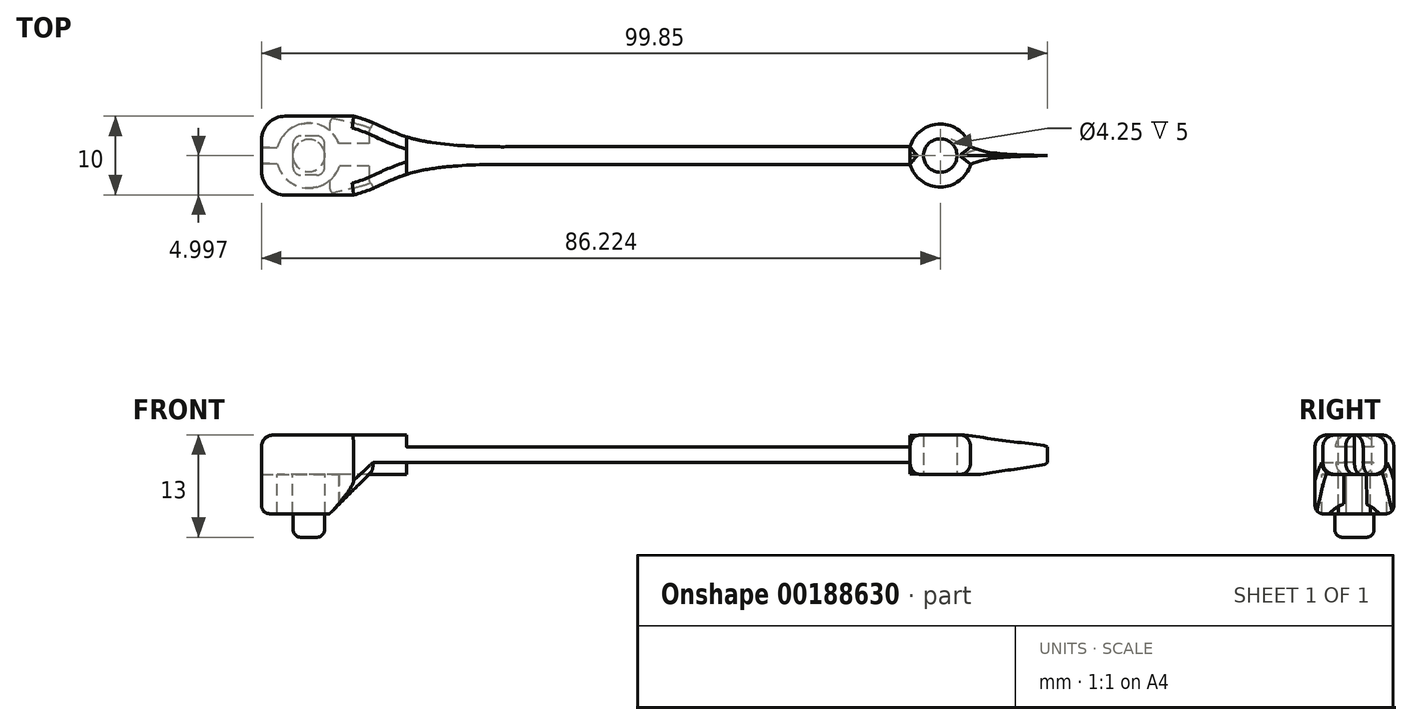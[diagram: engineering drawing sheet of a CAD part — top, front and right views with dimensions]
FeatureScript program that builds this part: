
annotation { "Feature Type Name" : "Feature", "Feature Type Description" : "" }
export const myFeature = defineFeature(function(context is Context, id is Id, definition is map)
    precondition{}
    {
        {
            var Q0;
            Q0=qCreatedBy(makeId("Top.planeOp"),FACE);
            var sketch = newSketch(context, id + "F0", { "sketchPlane" : qUnion([Q0])});
            skLineSegment(sketch, "E0.right", {"start": v(-50, 3.04) * mm, "end": v(-50, -0.96) * mm});
            skPoint(sketch, "E0.middle", {"position": v(0, 1.04) * mm});
            skLineSegment(sketch, "E1.bottom", {"start": v(-47, 6.04) * mm, "end": v(-38, 6.04) * mm});
            skLineSegment(sketch, "E1.top", {"start": v(-47, -3.96) * mm, "end": v(-38, -3.96) * mm});
            skLineSegment(sketch, "E1.right", {"start": v(-38, 6.04) * mm, "end": v(-38, 5.96) * mm});
            skFitSpline(sketch, "E2.MirrorCS", {"points": [v(-38.32, 6.04) * mm, v(-30.88, 3.21) * mm, v(-1.67, 3.16) * mm, v(36.22, 5.93) * mm, v(49.85, 2.13) * mm], "startDerivative": vector(52.94, -12.3) * mm, "endDerivative": vector(42.84, -21) * mm});
            skLineSegment(sketch, "E3.trimOffspring", {"start": v(-38, 6.04) * mm, "end": v(-47, 6.04) * mm});
            skPoint(sketch, "E4.orphan", {"position": v(50, 6.04) * mm});
            skLineSegment(sketch, "E5.trimOffspring", {"start": v(-38, -3.96) * mm, "end": v(-47, -3.96) * mm});
            skPoint(sketch, "E6.visualSharp", {"position": v(-50, 6.04) * mm});
            skArc(sketch, "E6.filletArc", {"start": v(-47, 6.04) * mm, "mid": v(-49.12, 5.16) * mm, "end": v(-50, 3.04) * mm});
            skPoint(sketch, "E7.visualSharp", {"position": v(-50, -3.96) * mm});
            skArc(sketch, "E7.filletArc", {"start": v(-50, -0.96) * mm, "mid": v(-49.12, -3.08) * mm, "end": v(-47, -3.96) * mm});
            skLineSegment(sketch, "E8", {"start": v(-18.95, 2.15) * mm, "end": v(32.38, 2.15) * mm});
            skFitSpline(sketch, "E9.MirrorCS", {"points": [v(-38.32, -3.97) * mm, v(-30.88, -1.14) * mm, v(-1.67, -1.09) * mm, v(36.22, -3.86) * mm, v(49.85, -0.06) * mm], "startDerivative": vector(52.94, 12.3) * mm, "endDerivative": vector(42.84, 21) * mm});
            skLineSegment(sketch, "E10.MirrorCS", {"start": v(-18.95, -0.08) * mm, "end": v(32.38, -0.08) * mm});
            skArc(sketch, "E11", {"start": v(40.06, 2.15) * mm, "mid": v(36.22, 5.04) * mm, "end": v(32.38, 2.15) * mm});
            skFitSpline(sketch, "E12", {"points": [v(40.06, 2.15) * mm, v(42.27, 1.49) * mm, v(49.85, 1.04) * mm], "startDerivative": vector(5.23, -2.09) * mm, "endDerivative": vector(13.53, -0.32) * mm});
            skFitSpline(sketch, "E13.MirrorCS", {"points": [v(40.06, -0.08) * mm, v(42.27, 0.59) * mm, v(49.85, 1.04) * mm], "startDerivative": vector(5.23, 2.09) * mm, "endDerivative": vector(13.53, 0.32) * mm});
            skCircle(sketch, "E14", {"center": v(36.22, 1.04) * mm, "radius": 2.12 * mm});
            skLineSegment(sketch, "E15.trimOffspring", {"start": v(40.06, -0.08) * mm, "end": v(49.84, -0.08) * mm});
            skArc(sketch, "E16.trimOffspring", {"start": v(32.38, -0.08) * mm, "mid": v(36.22, -2.96) * mm, "end": v(40.06, -0.08) * mm});
            skPoint(sketch, "E17.trimOffspring.end.orphan", {"position": v(49.84, 2.15) * mm});
            skPoint(sketch, "E18.start.orphan", {"position": v(-38, 1.04) * mm});
            skLineSegment(sketch, "E19.trimOffspring", {"start": v(-38, -3.89) * mm, "end": v(-38, -3.96) * mm});
            skPoint(sketch, "E20.startSnap0", {"position": v(-50, 1.04) * mm});
            skCircle(sketch, "E21", {"center": v(-43.9, 1.04) * mm, "radius": 2.12 * mm});
            skPoint(sketch, "E20.start.orphan", {"position": v(-49.8, 1.04) * mm});
            skSolve(sketch);
        }
        {
            var Q0;
            Q0=makeQuery(id+"F0.imprint","IMPRINT",FACE,{"disambiguationData":[TD([[makeQuery(id+"F0.imprint","IMPRINT",EDGE,{"derivedFrom":sQuery(id+"F0.wireOp",EDGE,"E0.right")}),1.0]])]});
            var Q1;
            Q1=makeQuery(id+"F0.imprint","IMPRINT",FACE,{"disambiguationData":[TD([[makeQuery(id+"F0.imprint","IMPRINT",EDGE,{"derivedFrom":sQuery(id+"F0.wireOp",EDGE,"E21")}),1.0]])]});
            extrude(context, id + "F1", {"entities" : qUnion([Q0, Q1]), "depth" : 5 * mm});
        }
        {
            var Q0;
            Q0=makeQuery(id+"F1.opExtrude","CAP_FACE",FACE,{"disambiguationData":[OSD([sQuery(id+"F0.wireOp",EDGE,"E0.right"),sQuery(id+"F0.wireOp",EDGE,"E2.MirrorCS"),sQuery(id+"F0.wireOp",EDGE,"E3.trimOffspring"),sQuery(id+"F0.wireOp",EDGE,"E5.trimOffspring"),sQuery(id+"F0.wireOp",EDGE,"E6.filletArc"),sQuery(id+"F0.wireOp",EDGE,"E7.filletArc"),sQuery(id+"F0.wireOp",EDGE,"E8"),sQuery(id+"F0.wireOp",EDGE,"E9.MirrorCS"),sQuery(id+"F0.wireOp",EDGE,"E10.MirrorCS"),sQuery(id+"F0.wireOp",EDGE,"E11"),sQuery(id+"F0.wireOp",EDGE,"E12"),sQuery(id+"F0.wireOp",EDGE,"E13.MirrorCS"),sQuery(id+"F0.wireOp",EDGE,"E14"),sQuery(id+"F0.wireOp",EDGE,"E16.trimOffspring")])],"isStart":false});
            var sketch = newSketch(context, id + "F2", { "sketchPlane" : qUnion([Q0])});
            skCircle(sketch, "E22", {"center": v(-44, 1.04) * mm, "radius": 2.05 * mm});
            skPoint(sketch, "E23.start.orphan", {"position": v(-50, 1.04) * mm});
            skPoint(sketch, "E24.trimOffspring.end.orphan", {"position": v(-37.98, 1.04) * mm});
            skArc(sketch, "E25", {"start": v(-40.17, 2.59) * mm, "mid": v(-48.12, 0.91) * mm, "end": v(-40.08, -0.28) * mm});
            skLineSegment(sketch, "E26", {"start": v(-35.34, 4.98) * mm, "end": v(-35.34, 2.53) * mm});
            skLineSegment(sketch, "E27.trimOffspring", {"start": v(-35.34, -0.28) * mm, "end": v(-35.34, -3.64) * mm});
            skLineSegment(sketch, "E28.0", {"start": v(-35.34, 2.53) * mm, "end": v(-40.17, 2.59) * mm});
            skLineSegment(sketch, "E29.0", {"start": v(-35.34, -0.28) * mm, "end": v(-40.08, -0.28) * mm});
            skSolve(sketch);
        }
        {
            var Q0;
            Q0 = qSketchRegion(id + "F2", true);
            var Q1;
            {var subQ2=sQuery(id+"F2.wireOp",EDGE,"E25");Q1=makeQuery(id+"F2.imprint","IMPRINT",FACE,{"disambiguationData":[TD([[makeQuery(id+"F2.imprint","IMPRINT",EDGE,{"derivedFrom":subQ2}),-1.0]])]});}
            extrude(context, id + "F3", {"entities" : qUnion([Q0, Q1]), "operationType" : NewBodyOperationType.ADD, "oppositeDirection" : true, "depth" : 10 * mm});
        }
        {
            var Q0;
            Q0=makeQuery(id+"F3.opExtrude","CAP_FACE",FACE,{"disambiguationData":[OSD([sQuery(id+"F2.wireOp",EDGE,"E22")])],"isStart":false});
            var sketch = newSketch(context, id + "F4", { "sketchPlane" : qUnion([Q0])});
            skLineSegment(sketch, "E30.bottom", {"start": v(-42, 1.46) * mm, "end": v(-46, 1.46) * mm});
            skLineSegment(sketch, "E30.top", {"start": v(-42, -3.54) * mm, "end": v(-46, -3.54) * mm});
            skLineSegment(sketch, "E30.left", {"start": v(-42, 1.46) * mm, "end": v(-42, -3.54) * mm});
            skLineSegment(sketch, "E30.right", {"start": v(-46, 1.46) * mm, "end": v(-46, -3.54) * mm});
            skPoint(sketch, "E30.middle", {"position": v(-44, -1.04) * mm});
            skSolve(sketch);
        }
        {
            var Q0;
            {var subQ0=sQuery(id+"F4.wireOp",EDGE,"E30.bottom");Q0=makeQuery(id+"F4.imprint","IMPRINT",FACE,{"disambiguationData":[TD([[makeQuery(id+"F4.imprint","IMPRINT",EDGE,{"derivedFrom":subQ0}),1.0]])]});}
            var Q1;
            {var subQ0=sQuery(id+"F4.wireOp",EDGE,"E30.top");Q1=makeQuery(id+"F4.imprint","IMPRINT",FACE,{"disambiguationData":[TD([[makeQuery(id+"F4.imprint","IMPRINT",EDGE,{"derivedFrom":subQ0}),-1.0]])]});}
            var Q2;
            {var subQ0=sQuery(id+"F4.wireOp",EDGE,"E30.left");var subQ1=makeQuery(id+"F3.opExtrude","CAP_EDGE",EDGE,{"disambiguationData":[OSD([sQuery(id+"F2.wireOp",EDGE,"E22")])],"isStart":false});var subQ2=makeQuery(id+"F4.imprint","INTERSECT",VERTEX,{"disambiguationData":[OD(0.0)],"derivedFrom":[subQ1,subQ0]});Q2=makeQuery(id+"F4.imprint","IMPRINT",FACE,{"disambiguationData":[TD([[makeQuery(id+"F4.imprint","IMPRINT",EDGE,{"disambiguationData":[TD([[subQ2,-1.0]])],"derivedFrom":subQ0}),-1.0]])]});}
            extrude(context, id + "F5", {"entities" : qUnion([Q0, Q1, Q2]), "operationType" : NewBodyOperationType.ADD, "depth" : 3 * mm});
        }
        {
            var Q0;
            Q0=makeQuery(id+"F5.opExtrude","CAP_EDGE",EDGE,{"disambiguationData":[OSD([sQuery(id+"F4.wireOp",EDGE,"E30.top")])],"isStart":false});
            var Q1;
            Q1=makeQuery(id+"F5.opExtrude","CAP_EDGE",EDGE,{"disambiguationData":[OSD([sQuery(id+"F4.wireOp",EDGE,"E30.right")])],"isStart":false});
            var Q2;
            Q2=makeQuery(id+"F5.opExtrude","CAP_EDGE",EDGE,{"disambiguationData":[OSD([sQuery(id+"F4.wireOp",EDGE,"E30.left")])],"isStart":false});
            var Q3;
            Q3=makeQuery(id+"F5.opExtrude","CAP_EDGE",EDGE,{"disambiguationData":[OSD([sQuery(id+"F4.wireOp",EDGE,"E30.bottom")])],"isStart":false});
            fillet(context, id + "F6", {"entities" : qUnion([Q0, Q1, Q2, Q3]), "radius" : 1 * mm, "tangentPropagation" : true, "allowEdgeOverflow" : false});
        }
        {
            var Q0;
            Q0=makeQuery(id+"F5.opExtrude","SWEPT_EDGE",EDGE,{"disambiguationData":[OSD([sQuery(id+"F4.wireOp",EDGE,"E30.top"),sQuery(id+"F4.wireOp",EDGE,"E30.right")])]});
            var Q1;
            Q1=makeQuery(id+"F5.opExtrude","SWEPT_EDGE",EDGE,{"disambiguationData":[OSD([sQuery(id+"F4.wireOp",EDGE,"E30.top"),sQuery(id+"F4.wireOp",EDGE,"E30.left")])]});
            var Q2;
            Q2=makeQuery(id+"F5.opExtrude","SWEPT_EDGE",EDGE,{"disambiguationData":[OSD([sQuery(id+"F4.wireOp",EDGE,"E30.bottom"),sQuery(id+"F4.wireOp",EDGE,"E30.left")])]});
            var Q3;
            Q3=makeQuery(id+"F5.opExtrude","SWEPT_EDGE",EDGE,{"disambiguationData":[OSD([sQuery(id+"F4.wireOp",EDGE,"E30.bottom"),sQuery(id+"F4.wireOp",EDGE,"E30.right")])]});
            fillet(context, id + "F7", {"entities" : qUnion([Q0, Q1, Q2, Q3]), "radius" : 1 * mm, "tangentPropagation" : true, "allowEdgeOverflow" : false});
        }
        {
            var Q0;
            Q0=makeQuery(id+"F1.opExtrude","CAP_EDGE",EDGE,{"disambiguationData":[OSD([sQuery(id+"F0.wireOp",EDGE,"E2.MirrorCS")])],"isStart":true});
            var Q1;
            Q1=makeQuery(id+"F1.opExtrude","CAP_EDGE",EDGE,{"disambiguationData":[OSD([sQuery(id+"F0.wireOp",EDGE,"E8")])],"isStart":true});
            var Q2;
            Q2=makeQuery(id+"F1.opExtrude","CAP_EDGE",EDGE,{"disambiguationData":[OSD([sQuery(id+"F0.wireOp",EDGE,"E8")])],"isStart":false});
            var Q3;
            Q3=makeQuery(id+"F1.opExtrude","CAP_EDGE",EDGE,{"disambiguationData":[OSD([sQuery(id+"F0.wireOp",EDGE,"E2.MirrorCS")])],"isStart":false});
            var Q4;
            Q4=makeQuery(id+"F1.opExtrude","CAP_EDGE",EDGE,{"disambiguationData":[OSD([sQuery(id+"F0.wireOp",EDGE,"E3.trimOffspring")])],"isStart":false});
            var Q5;
            Q5=makeQuery(id+"F1.opExtrude","CAP_EDGE",EDGE,{"disambiguationData":[OSD([sQuery(id+"F0.wireOp",EDGE,"E6.filletArc")])],"isStart":false});
            var Q6;
            Q6=makeQuery(id+"F1.opExtrude","CAP_EDGE",EDGE,{"disambiguationData":[OSD([sQuery(id+"F0.wireOp",EDGE,"E11")])],"isStart":false});
            var Q7;
            Q7=makeQuery(id+"F1.opExtrude","CAP_EDGE",EDGE,{"disambiguationData":[OSD([sQuery(id+"F0.wireOp",EDGE,"E11")])],"isStart":true});
            var Q8;
            Q8=makeQuery(id+"F1.opExtrude","CAP_EDGE",EDGE,{"disambiguationData":[OSD([sQuery(id+"F0.wireOp",EDGE,"E12")])],"isStart":false});
            var Q9;
            Q9=makeQuery(id+"F1.opExtrude","CAP_EDGE",EDGE,{"disambiguationData":[OSD([sQuery(id+"F0.wireOp",EDGE,"E16.trimOffspring")])],"isStart":true});
            var Q10;
            Q10=makeQuery(id+"F1.opExtrude","CAP_EDGE",EDGE,{"disambiguationData":[OSD([sQuery(id+"F0.wireOp",EDGE,"E10.MirrorCS")])],"isStart":true});
            var Q11;
            Q11=makeQuery(id+"F1.opExtrude","CAP_EDGE",EDGE,{"disambiguationData":[OSD([sQuery(id+"F0.wireOp",EDGE,"E13.MirrorCS")])],"isStart":true});
            var Q12;
            Q12=makeQuery(id+"F1.opExtrude","CAP_EDGE",EDGE,{"disambiguationData":[OSD([sQuery(id+"F0.wireOp",EDGE,"E10.MirrorCS")])],"isStart":false});
            var Q13;
            Q13=makeQuery(id+"F1.opExtrude","CAP_EDGE",EDGE,{"disambiguationData":[OSD([sQuery(id+"F0.wireOp",EDGE,"E16.trimOffspring")])],"isStart":false});
            var Q14;
            Q14=makeQuery(id+"F1.opExtrude","CAP_EDGE",EDGE,{"disambiguationData":[OSD([sQuery(id+"F0.wireOp",EDGE,"E13.MirrorCS")])],"isStart":false});
            var Q15;
            Q15=makeQuery(id+"F1.opExtrude","CAP_EDGE",EDGE,{"disambiguationData":[OSD([sQuery(id+"F0.wireOp",EDGE,"E9.MirrorCS")])],"isStart":true});
            var Q16;
            Q16=makeQuery(id+"F1.opExtrude","CAP_EDGE",EDGE,{"disambiguationData":[OSD([sQuery(id+"F0.wireOp",EDGE,"E9.MirrorCS")])],"isStart":false});
            fillet(context, id + "F8", {"entities" : qUnion([Q0, Q1, Q2, Q3, Q4, Q5, Q6, Q7, Q8, Q9, Q10, Q11, Q12, Q13, Q14, Q15, Q16]), "radius" : 1.5 * mm, "tangentPropagation" : true, "allowEdgeOverflow" : false});
        }
        {
            var Q0;
            Q0=makeQuery(id+"F3.opExtrude","CAP_EDGE",EDGE,{"disambiguationData":[OSD([sQuery(id+"F2.wireOp",EDGE,"E27.trimOffspring")])],"isStart":false});
            var Q1;
            Q1=makeQuery(id+"F3.opExtrude","CAP_EDGE",EDGE,{"disambiguationData":[OSD([sQuery(id+"F2.wireOp",EDGE,"E26")])],"isStart":false});
            chamfer(context, id + "F9", {"entities" : qUnion([Q0, Q1]), "width" : 6 * mm, "tangentPropagation" : true});
        }
        {
            var Q0;
            {var subQ0=sQuery(id+"F0.wireOp",EDGE,"E5.trimOffspring");Q0=makeQuery(id+"F9.opChamfer","BLEND_EDGE",EDGE,{"blendedFrom":[makeQuery(id+"F3.opExtrude","CAP_EDGE",EDGE,{"disambiguationData":[OSD([sQuery(id+"F2.wireOp",EDGE,"E27.trimOffspring")])],"isStart":false}),makeQuery(id+"F3.boolean.opBoolean","MERGE",FACE,{"derivedFrom":[makeQuery(id+"F1.opExtrude","SWEPT_FACE",FACE,{"disambiguationData":[OSD([subQ0])]}),makeQuery(id+"F3.opExtrude","SWEPT_FACE",FACE,{"disambiguationData":[OSD([subQ0])]})]})],"blendedInto":[makeQuery(id+"F3.boolean.opBoolean","MERGE",FACE,{"derivedFrom":[makeQuery(id+"F1.opExtrude","SWEPT_FACE",FACE,{"disambiguationData":[OSD([subQ0])]}),makeQuery(id+"F3.opExtrude","SWEPT_FACE",FACE,{"disambiguationData":[OSD([subQ0])]})]})]});}
            var Q1;
            Q1=makeQuery(id+"F3.opExtrude","CAP_EDGE",EDGE,{"disambiguationData":[OSD([sQuery(id+"F0.wireOp",EDGE,"E5.trimOffspring")])],"isStart":false});
            var Q2;
            Q2=makeQuery(id+"F3.opExtrude","CAP_EDGE",EDGE,{"disambiguationData":[OSD([sQuery(id+"F0.wireOp",EDGE,"E7.filletArc")])],"isStart":false});
            var Q3;
            Q3=makeQuery(id+"F3.opExtrude","CAP_EDGE",EDGE,{"disambiguationData":[OSD([sQuery(id+"F0.wireOp",EDGE,"E0.right")])],"isStart":false});
            var Q4;
            Q4=makeQuery(id+"F3.opExtrude","CAP_EDGE",EDGE,{"disambiguationData":[OSD([sQuery(id+"F0.wireOp",EDGE,"E6.filletArc")])],"isStart":false});
            var Q5;
            Q5=makeQuery(id+"F3.opExtrude","CAP_EDGE",EDGE,{"disambiguationData":[OSD([sQuery(id+"F0.wireOp",EDGE,"E3.trimOffspring")])],"isStart":false});
            var Q6;
            {var subQ0=sQuery(id+"F0.wireOp",EDGE,"E3.trimOffspring");Q6=makeQuery(id+"F9.opChamfer","BLEND_EDGE",EDGE,{"blendedFrom":[makeQuery(id+"F3.opExtrude","CAP_EDGE",EDGE,{"disambiguationData":[OSD([sQuery(id+"F2.wireOp",EDGE,"E26")])],"isStart":false}),makeQuery(id+"F3.boolean.opBoolean","MERGE",FACE,{"derivedFrom":[makeQuery(id+"F1.opExtrude","SWEPT_FACE",FACE,{"disambiguationData":[OSD([subQ0])]}),makeQuery(id+"F3.opExtrude","SWEPT_FACE",FACE,{"disambiguationData":[OSD([subQ0])]})]})],"blendedInto":[makeQuery(id+"F3.boolean.opBoolean","MERGE",FACE,{"derivedFrom":[makeQuery(id+"F1.opExtrude","SWEPT_FACE",FACE,{"disambiguationData":[OSD([subQ0])]}),makeQuery(id+"F3.opExtrude","SWEPT_FACE",FACE,{"disambiguationData":[OSD([subQ0])]})]})]});}
            var Q7;
            {var subQ0=sQuery(id+"F0.wireOp",EDGE,"E2.MirrorCS");Q7=makeQuery(id+"F9.opChamfer","BLEND_EDGE",EDGE,{"blendedFrom":[makeQuery(id+"F3.opExtrude","CAP_EDGE",EDGE,{"disambiguationData":[OSD([sQuery(id+"F2.wireOp",EDGE,"E26")])],"isStart":false}),makeQuery(id+"F3.boolean.opBoolean","MERGE",FACE,{"derivedFrom":[makeQuery(id+"F1.opExtrude","SWEPT_FACE",FACE,{"disambiguationData":[OSD([subQ0])]}),makeQuery(id+"F3.opExtrude","SWEPT_FACE",FACE,{"disambiguationData":[OSD([subQ0])]})]})],"blendedInto":[makeQuery(id+"F3.boolean.opBoolean","MERGE",FACE,{"derivedFrom":[makeQuery(id+"F1.opExtrude","SWEPT_FACE",FACE,{"disambiguationData":[OSD([subQ0])]}),makeQuery(id+"F3.opExtrude","SWEPT_FACE",FACE,{"disambiguationData":[OSD([subQ0])]})]})]});}
            var Q8;
            {var subQ0=sQuery(id+"F0.wireOp",EDGE,"E9.MirrorCS");Q8=makeQuery(id+"F9.opChamfer","BLEND_EDGE",EDGE,{"blendedFrom":[makeQuery(id+"F3.opExtrude","CAP_EDGE",EDGE,{"disambiguationData":[OSD([sQuery(id+"F2.wireOp",EDGE,"E27.trimOffspring")])],"isStart":false}),makeQuery(id+"F3.boolean.opBoolean","MERGE",FACE,{"derivedFrom":[makeQuery(id+"F1.opExtrude","SWEPT_FACE",FACE,{"disambiguationData":[OSD([subQ0])]}),makeQuery(id+"F3.opExtrude","SWEPT_FACE",FACE,{"disambiguationData":[OSD([subQ0])]})]})],"blendedInto":[makeQuery(id+"F3.boolean.opBoolean","MERGE",FACE,{"derivedFrom":[makeQuery(id+"F1.opExtrude","SWEPT_FACE",FACE,{"disambiguationData":[OSD([subQ0])]}),makeQuery(id+"F3.opExtrude","SWEPT_FACE",FACE,{"disambiguationData":[OSD([subQ0])]})]})]});}
            fillet(context, id + "F10", {"entities" : qUnion([Q0, Q1, Q2, Q3, Q4, Q5, Q6, Q7, Q8]), "radius" : 1 * mm, "tangentPropagation" : true, "allowEdgeOverflow" : false});
        }
        {
            var Q0;
            Q0=makeQuery(id+"F1.opExtrude","SWEPT_FACE",FACE,{"disambiguationData":[OSD([sQuery(id+"F0.wireOp",EDGE,"E10.MirrorCS")])]});
            var sketch = newSketch(context, id + "F11", { "sketchPlane" : qUnion([Q0])});
            skLineSegment(sketch, "E31.bottom", {"start": v(-18.95, 3.5) * mm, "end": v(32.38, 3.5) * mm});
            skLineSegment(sketch, "E31.top", {"start": v(-31.6, 1.5) * mm, "end": v(32.38, 1.5) * mm});
            skLineSegment(sketch, "E32.top", {"start": v(-31.6, -3.32) * mm, "end": v(32.38, -3.32) * mm});
            skLineSegment(sketch, "E32.left", {"start": v(-31.6, 1.5) * mm, "end": v(-31.6, -3.32) * mm});
            skLineSegment(sketch, "E32.right", {"start": v(32.38, 1.5) * mm, "end": v(32.38, -3.32) * mm});
            skLineSegment(sketch, "E33.bottom", {"start": v(-31.6, 3.5) * mm, "end": v(32.38, 3.5) * mm});
            skLineSegment(sketch, "E33.top", {"start": v(-31.6, 10.87) * mm, "end": v(32.38, 10.87) * mm});
            skLineSegment(sketch, "E33.left", {"start": v(-31.6, 3.5) * mm, "end": v(-31.6, 10.87) * mm});
            skLineSegment(sketch, "E33.right", {"start": v(32.38, 3.5) * mm, "end": v(32.38, 10.87) * mm});
            skSolve(sketch);
        }
        {
            var Q0;
            Q0 = qSketchRegion(id + "F11", true);
            extrude(context, id + "F12", {"entities" : qUnion([Q0]), "operationType" : NewBodyOperationType.REMOVE, "endBound" : BoundingType.SYMMETRIC, "oppositeDirection" : true, "depth" : 7 * mm});
        }
        {
            var Q0;
            Q0=makeQuery(id+"F10.opFillet","SPLIT",FACE,{"disambiguationData":[OD(2.0)],"derivedFrom":makeQuery(id+"F3.opExtrude","CAP_FACE",FACE,{"disambiguationData":[OSD([sQuery(id+"F0.wireOp",EDGE,"E0.right"),sQuery(id+"F0.wireOp",EDGE,"E2.MirrorCS"),sQuery(id+"F0.wireOp",EDGE,"E3.trimOffspring"),sQuery(id+"F0.wireOp",EDGE,"E5.trimOffspring"),sQuery(id+"F0.wireOp",EDGE,"E6.filletArc"),sQuery(id+"F0.wireOp",EDGE,"E7.filletArc"),sQuery(id+"F0.wireOp",EDGE,"E9.MirrorCS"),sQuery(id+"F2.wireOp",EDGE,"E25"),sQuery(id+"F2.wireOp",EDGE,"E26"),sQuery(id+"F2.wireOp",EDGE,"E27.trimOffspring"),sQuery(id+"F2.wireOp",EDGE,"E28.0"),sQuery(id+"F2.wireOp",EDGE,"E29.0")])],"isStart":false})});
            var sketch = newSketch(context, id + "F13", { "sketchPlane" : qUnion([Q0])});
            skLineSegment(sketch, "E34", {"start": v(-49, -1.04) * mm, "end": v(-46.99, -1.04) * mm});
            skLineSegment(sketch, "E35.0", {"start": v(-49, -2.04) * mm, "end": v(-46.99, -2.04) * mm});
            skLineSegment(sketch, "E36.0", {"start": v(-49, -0.04) * mm, "end": v(-46.99, -0.04) * mm});
            skLineSegment(sketch, "E37.bottom", {"start": v(-46.99, -0.04) * mm, "end": v(-51.01, -0.04) * mm});
            skLineSegment(sketch, "E37.top", {"start": v(-46.99, -2.04) * mm, "end": v(-51.01, -2.04) * mm});
            skLineSegment(sketch, "E37.left", {"start": v(-46.99, -0.04) * mm, "end": v(-46.99, -2.04) * mm});
            skLineSegment(sketch, "E37.right", {"start": v(-51.01, -0.04) * mm, "end": v(-51.01, -2.04) * mm});
            skPoint(sketch, "E37.middle", {"position": v(-49, -1.04) * mm});
            skSolve(sketch);
        }
        {
            var Q0;
            Q0 = qSketchRegion(id + "F13", true);
            extrude(context, id + "F14", {"entities" : qUnion([Q0]), "operationType" : NewBodyOperationType.REMOVE, "oppositeDirection" : true, "depth" : 5 * mm});
        }
    });
